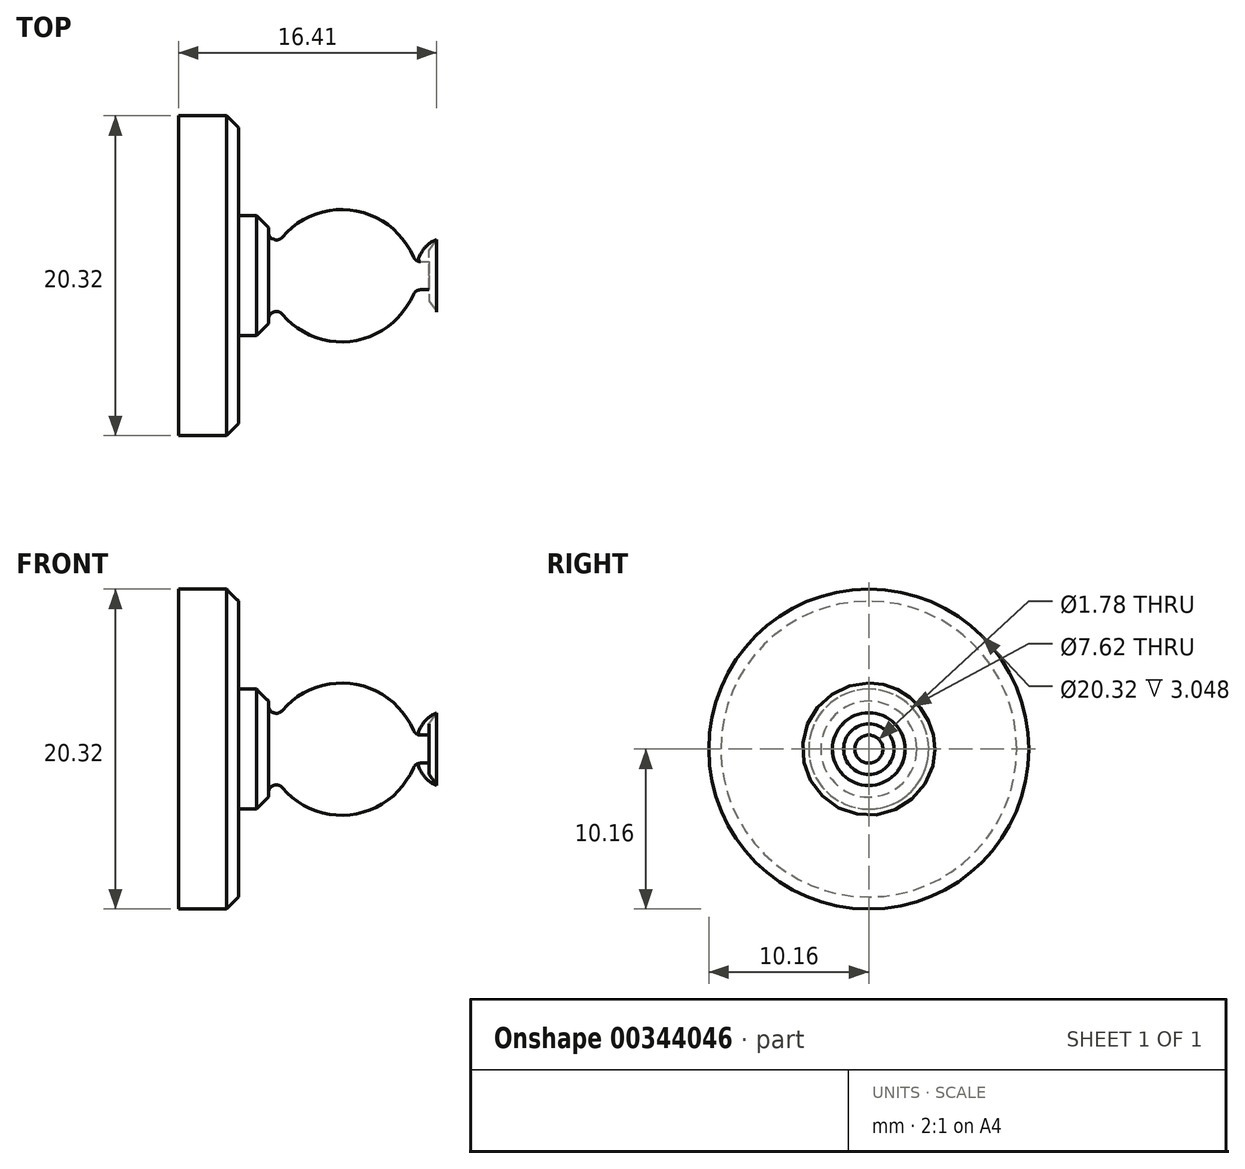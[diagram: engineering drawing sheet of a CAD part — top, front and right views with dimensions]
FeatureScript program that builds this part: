
annotation { "Feature Type Name" : "Feature", "Feature Type Description" : "" }
export const myFeature = defineFeature(function(context is Context, id is Id, definition is map)
    precondition{}
    {
        {
            var Q0;
            Q0=qCreatedBy(makeId("Front.planeOp"),FACE);
            var sketch = newSketch(context, id + "F0", { "sketchPlane" : qUnion([Q0])});
            skLineSegment(sketch, "E0", {"start": v(0, 0) * mm, "end": v(-19.05, 0) * mm});
            skLineSegment(sketch, "E1", {"start": v(-19.05, 0) * mm, "end": v(-19.05, 10.16) * mm});
            skLineSegment(sketch, "E2", {"start": v(-19.05, 10.16) * mm, "end": v(-15.24, 10.16) * mm});
            skArc(sketch, "E3", {"start": v(0, 0) * mm, "mid": v(-0.84, 2.13) * mm, "end": v(-3.12, 2.03) * mm});
            skPoint(sketch, "E4.end.orphan", {"position": v(-2.51, 0.9) * mm});
            skPoint(sketch, "E5.start.orphan", {"position": v(-3.12, 0.9) * mm});
            skLineSegment(sketch, "E6", {"start": v(-3.12, 2.03) * mm, "end": v(-3.12, 0.9) * mm});
            skLineSegment(sketch, "E7", {"start": v(-3.12, 0.9) * mm, "end": v(-4, 0.9) * mm});
            skLineSegment(sketch, "E8", {"start": v(-15.24, 10.16) * mm, "end": v(-15.24, 3.81) * mm});
            skLineSegment(sketch, "E9", {"start": v(-15.24, 3.81) * mm, "end": v(-13.33, 3.81) * mm});
            skLineSegment(sketch, "E10", {"start": v(-13.33, 3.81) * mm, "end": v(-13.33, 0.89) * mm});
            skArc(sketch, "E11", {"start": v(-4, 0.9) * mm, "mid": v(-8.67, 4.2) * mm, "end": v(-13.33, 0.89) * mm});
            skSolve(sketch);
        }
        {
            var Q0;
            Q0=makeQuery(id+"F0.imprint","IMPRINT",FACE,{"disambiguationData":[TD([[makeQuery(id+"F0.imprint","IMPRINT",EDGE,{"derivedFrom":sQuery(id+"F0.wireOp",EDGE,"E0")}),-1.0]])]});
            var Q1;
            Q1=sQuery(id+"F0.wireOp",EDGE,"E0");
            revolve(context, id + "F1", {"entities" : qUnion([Q0]), "axis" : qUnion([Q1]), "revolveType" : RevolveType.FULL});
        }
        {
            var Q0;
            Q0=makeQuery(id+"F1.opRevolve","SWEPT_FACE",FACE,{"disambiguationData":[OSD([sQuery(id+"F0.wireOp",EDGE,"E11")])]});
            fillet(context, id + "F2", {"entities" : qUnion([Q0]), "radius" : 0.5 * mm, "tangentPropagation" : true, "allowEdgeOverflow" : false});
        }
        {
            var Q0;
            Q0=makeQuery(id+"F1.opRevolve","SWEPT_EDGE",EDGE,{"disambiguationData":[OSD([sQuery(id+"F0.wireOp",EDGE,"E2"),sQuery(id+"F0.wireOp",EDGE,"E8")])]});
            var Q1;
            Q1=makeQuery(id+"F1.opRevolve","SWEPT_EDGE",EDGE,{"disambiguationData":[OSD([sQuery(id+"F0.wireOp",EDGE,"E9"),sQuery(id+"F0.wireOp",EDGE,"E10")])]});
            var Q2;
            Q2=makeQuery(id+"F1.opRevolve","SWEPT_EDGE",EDGE,{"disambiguationData":[OSD([sQuery(id+"F0.wireOp",EDGE,"E3"),sQuery(id+"F0.wireOp",EDGE,"E6")])]});
            chamfer(context, id + "F3", {"entities" : qUnion([Q0, Q1, Q2]), "width" : 0.76 * mm, "tangentPropagation" : true});
        }
    });
